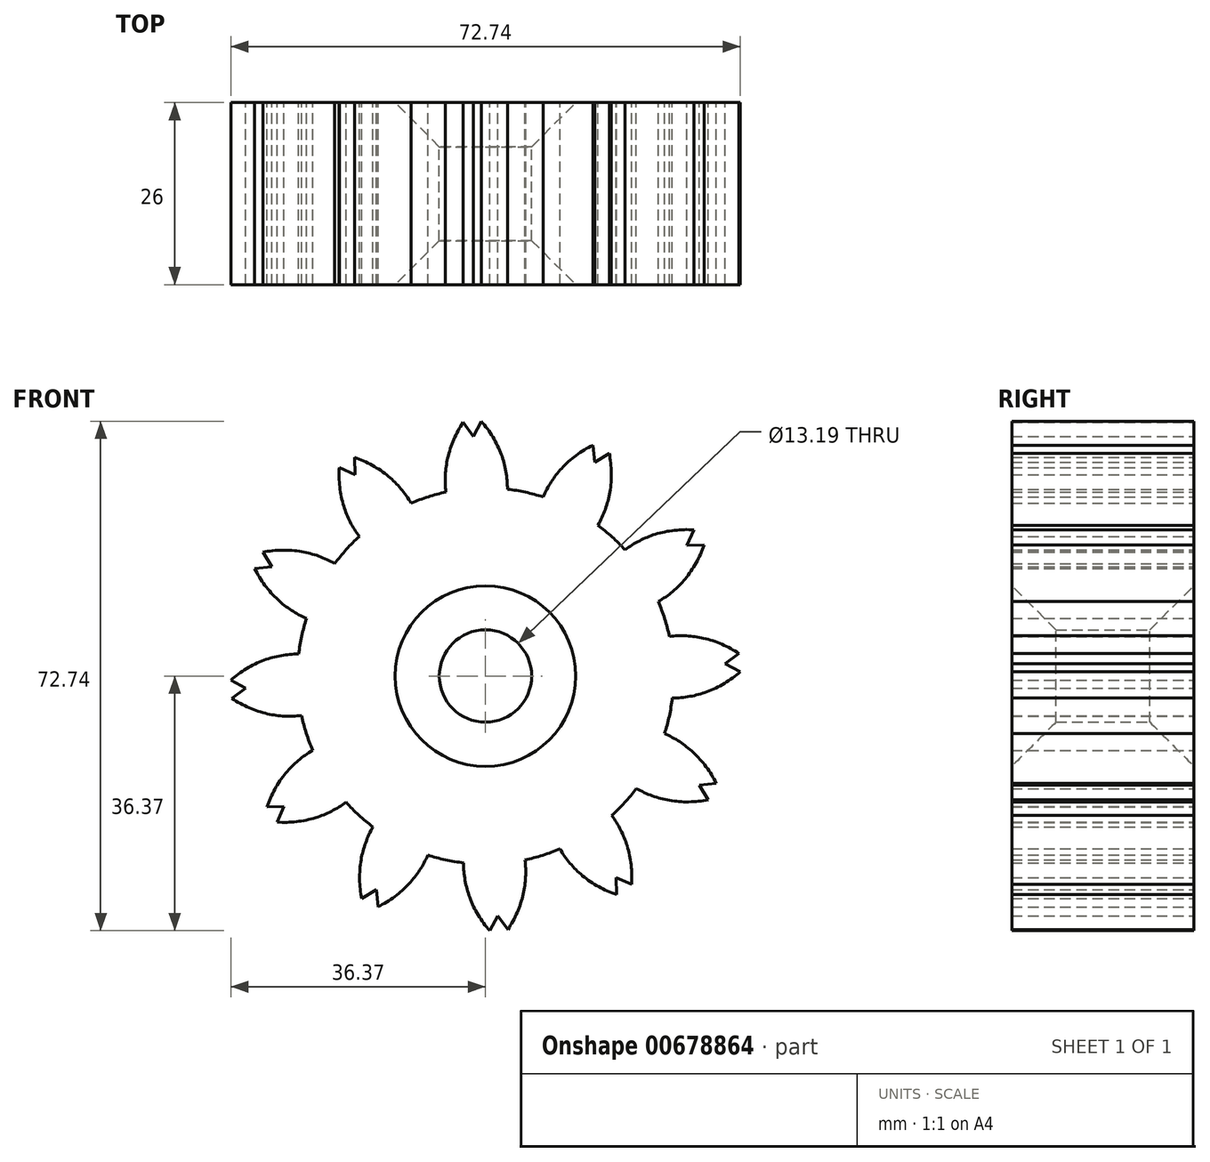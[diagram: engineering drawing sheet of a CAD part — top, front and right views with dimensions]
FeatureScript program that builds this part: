
annotation { "Feature Type Name" : "Feature", "Feature Type Description" : "" }
export const myFeature = defineFeature(function(context is Context, id is Id, definition is map)
    precondition{}
    {
        {
            var Q0;
            Q0=qCreatedBy(makeId("Front.planeOp"),FACE);
            var sketch = newSketch(context, id + "F0", { "sketchPlane" : qUnion([Q0])});
            skCircle(sketch, "E0", {"center": v(0, 0) * mm, "radius": 26.86 * mm});
            skCircle(sketch, "E1", {"center": v(0, 0) * mm, "radius": 29.34 * mm, "construction": true});
            skCircle(sketch, "E2", {"center": v(0, 0) * mm, "radius": 31.75 * mm, "construction": true});
            skLineSegment(sketch, "E3", {"start": v(0, 0) * mm, "end": v(0, 90.81) * mm, "construction": true});
            skLineSegment(sketch, "E4", {"start": v(0, 0) * mm, "end": v(-3.44, 104.98) * mm, "construction": true});
            skLineSegment(sketch, "E5", {"start": v(0, 29.34) * mm, "end": v(-81.02, 29.34) * mm, "construction": true});
            skLineSegment(sketch, "E6", {"start": v(0, 29.34) * mm, "end": v(-81.14, 15.03) * mm, "construction": true});
            skCircle(sketch, "E7", {"center": v(0, 0) * mm, "radius": 28.9 * mm, "construction": true});
            skCircle(sketch, "E8", {"center": v(0, 29.34) * mm, "radius": 7.3 * mm, "construction": true});
            skCircle(sketch, "E9", {"center": v(-7.2, 28.07) * mm, "radius": 7.3 * mm, "construction": true});
            skArc(sketch, "E10", {"start": v(2.26, 31.61) * mm, "mid": v(1.05, 34.12) * mm, "end": v(-0.6, 36.37) * mm});
            skArc(sketch, "E11", {"start": v(3.14, 26.65) * mm, "mid": v(2.91, 29.17) * mm, "end": v(2.26, 31.61) * mm});
            skArc(sketch, "E12.MirrorCS", {"start": v(-5.63, 26.08) * mm, "mid": v(-5.73, 28.6) * mm, "end": v(-5.4, 31.11) * mm});
            skArc(sketch, "E13.MirrorCS", {"start": v(-5.4, 31.11) * mm, "mid": v(-4.53, 33.76) * mm, "end": v(-3.19, 36.2) * mm});
            skLineSegment(sketch, "E14", {"start": v(-3.19, 36.2) * mm, "end": v(-1.76, 34.23) * mm});
            skLineSegment(sketch, "E15", {"start": v(-1.76, 34.23) * mm, "end": v(-0.6, 36.37) * mm});
            skCircle(sketch, "E16", {"center": v(0, 0) * mm, "radius": 6.6 * mm});
            skSolve(sketch);
        }
        {
            var Q0;
            Q0 = qSketchRegion(id + "F0", true);
            var Q1;
            Q1=makeQuery(id+"F0.imprint","IMPRINT",FACE,{"disambiguationData":[TD([[makeQuery(id+"F0.imprint","IMPRINT",EDGE,{"derivedFrom":sQuery(id+"F0.wireOp",EDGE,"67685d92-93bb-4960-9097-ca6fd6cf1b42.0")}),-1.0]])]});
            extrude(context, id + "F1", {"entities" : qUnion([Q0, Q1]), "depth" : 26 * mm, "offsetDistance" : 25 * mm});
        }
        {
            var Q0;
            Q0=makeQuery(id+"F1.opExtrude","SWEPT_BODY",BODY,{"disambiguationData":[OSD([sQuery(id+"F0.wireOp",EDGE,"E0"),sQuery(id+"F0.wireOp",EDGE,"67685d92-93bb-4960-9097-ca6fd6cf1b42.0"),sQuery(id+"F0.wireOp",EDGE,"67685d92-93bb-4960-9097-ca6fd6cf1b42.1"),sQuery(id+"F0.wireOp",EDGE,"67685d92-93bb-4960-9097-ca6fd6cf1b42.2"),sQuery(id+"F0.wireOp",EDGE,"E10"),sQuery(id+"F0.wireOp",EDGE,"E11"),sQuery(id+"F0.wireOp",EDGE,"E12.MirrorCS"),sQuery(id+"F0.wireOp",EDGE,"E13.MirrorCS"),sQuery(id+"F0.wireOp",EDGE,"E14"),sQuery(id+"F0.wireOp",EDGE,"E15")])]});
            var Q1;
            Q1=makeQuery(id+"F1.opExtrude","SWEPT_FACE",FACE,{"disambiguationData":[OSD([sQuery(id+"F0.wireOp",EDGE,"E0")])]});
            circularPattern(context, id + "F2", {"operationType" : NewBodyOperationType.ADD, "entities" : qUnion([Q0]), "axis" : qUnion([Q1]), "angle" : 360 * degree, "instanceCount" : 12, "equalSpace" : true});
        }
        {
            var Q0;
            Q0=makeQuery(id+"F1.opExtrude","SWEPT_FACE",FACE,{"disambiguationData":[OSD([sQuery(id+"F0.wireOp",EDGE,"E16")])]});
            chamfer(context, id + "F3", {"entities" : qUnion([Q0]), "width" : 6.3 * mm, "tangentPropagation" : true});
        }
    });
